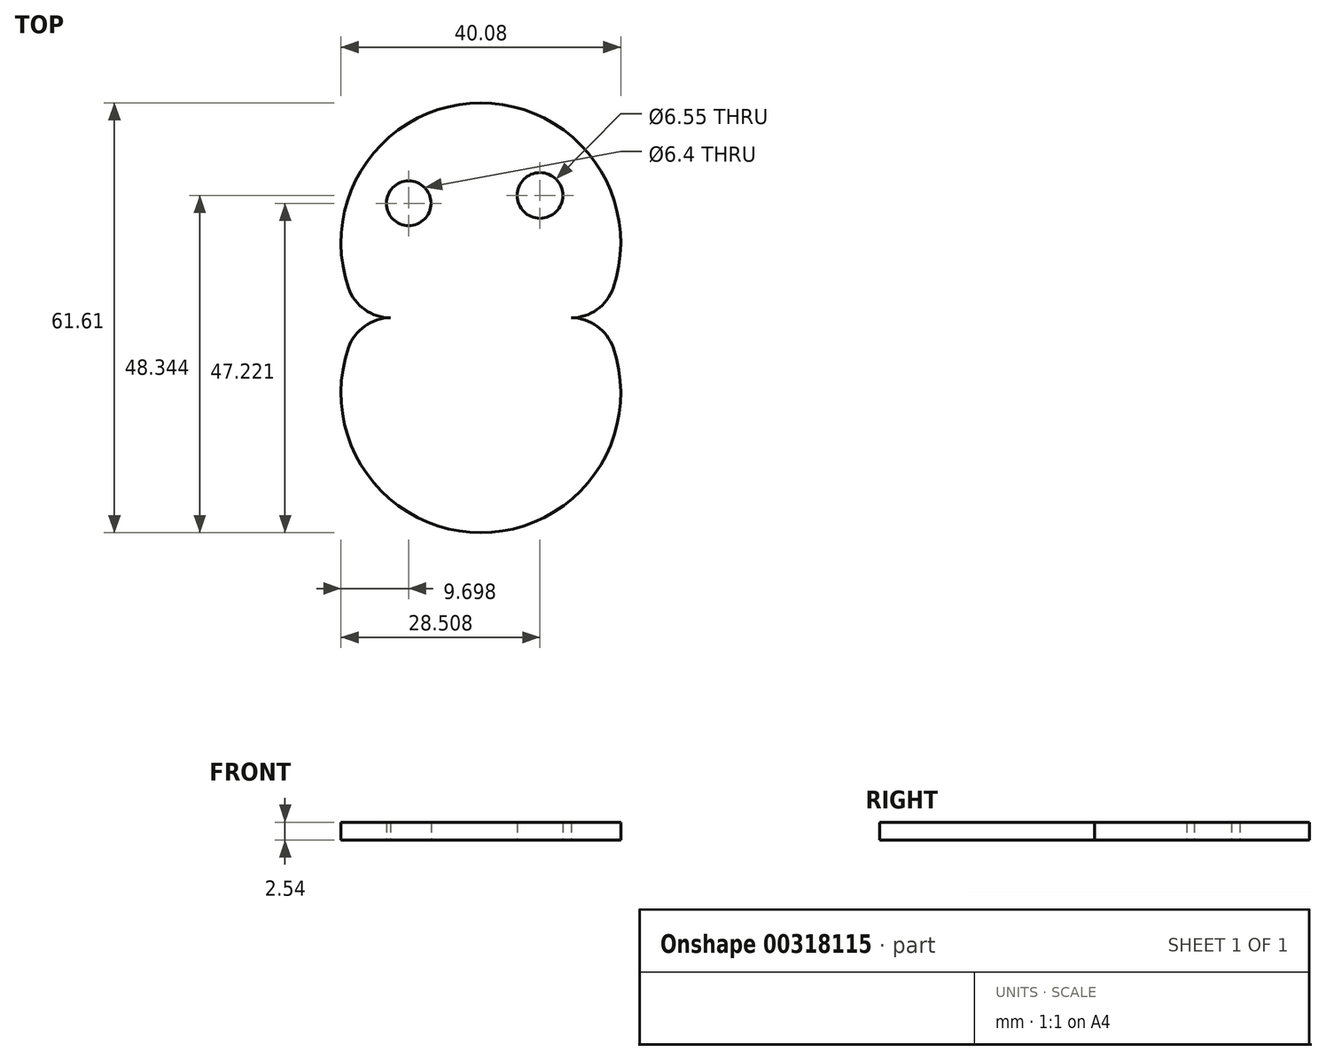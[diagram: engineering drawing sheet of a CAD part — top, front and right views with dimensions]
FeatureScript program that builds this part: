
annotation { "Feature Type Name" : "Feature", "Feature Type Description" : "" }
export const myFeature = defineFeature(function(context is Context, id is Id, definition is map)
    precondition{}
    {
        {
            var Q0;
            Q0=qCreatedBy(makeId("Top.planeOp"),FACE);
            var sketch = newSketch(context, id + "F0", { "sketchPlane" : qUnion([Q0])});
            skArc(sketch, "E0.0.startCap", {"start": v(-52.87, 18.11) * mm, "mid": v(-56.57, 19.3) * mm, "end": v(-58.88, 22.42) * mm});
            skArc(sketch, "E0.0.endCap", {"start": v(-20.94, 22.42) * mm, "mid": v(-23.26, 19.3) * mm, "end": v(-26.95, 18.11) * mm});
            skArc(sketch, "E0.1.startCap", {"start": v(-20.94, 22.42) * mm, "mid": v(-23.26, 19.3) * mm, "end": v(-26.95, 18.11) * mm});
            skArc(sketch, "E0.1.endCap", {"start": v(-52.87, 18.11) * mm, "mid": v(-56.57, 19.3) * mm, "end": v(-58.88, 22.42) * mm});
            skArc(sketch, "E0.1.right", {"start": v(-20.94, 22.42) * mm, "mid": v(-39.91, 48.92) * mm, "end": v(-58.88, 22.42) * mm});
            skArc(sketch, "E1.MirrorCS", {"start": v(-20.94, 13.81) * mm, "mid": v(-39.91, -12.7) * mm, "end": v(-58.88, 13.81) * mm});
            skArc(sketch, "E2.MirrorCS", {"start": v(-20.94, 13.81) * mm, "mid": v(-23.26, 16.93) * mm, "end": v(-26.95, 18.11) * mm});
            skArc(sketch, "E3.MirrorCS", {"start": v(-52.87, 18.11) * mm, "mid": v(-56.57, 16.93) * mm, "end": v(-58.88, 13.81) * mm});
            skFitSpline(sketch, "E4", {"points": [v(27.77, 29.98) * mm, v(33.3, 38.07) * mm, v(39.18, 29.61) * mm, v(48.74, 28.88) * mm, v(49.48, 20.05) * mm, v(38.44, 17.84) * mm, v(39.18, 10.48) * mm, v(42.86, 4.23) * mm, v(45.43, -6.44) * mm, v(41.02, -14.9) * mm, v(42.12, -21.52) * mm, v(34.4, -15.63) * mm, v(38.44, -8.28) * mm, v(30.72, -7.54) * mm, v(31.08, -22.26) * mm, v(24.46, -17.84) * mm, v(26.67, -5.33) * mm, v(19.68, -5.7) * mm, v(18.2, -20.05) * mm, v(13.43, -18.58) * mm, v(16, -6.44) * mm, v(12.7, -6.07) * mm, v(7.9, -18.58) * mm, v(7.9, -11.22) * mm, v(9.38, -5.33) * mm, v(14.53, 7.54) * mm, v(8.94, 10.65) * mm, v(9.53, 17.2) * mm, v(11.96, 10.85) * mm, v(18.94, 13.8) * mm, v(28.14, 7.9) * mm, v(31.08, 13.8) * mm, v(28.14, 22.62) * mm, v(23.73, 25.93) * mm, v(27.77, 29.98) * mm]});
            skCircle(sketch, "E5", {"center": v(-50.25, 34.53) * mm, "radius": 3.2 * mm});
            skCircle(sketch, "E6", {"center": v(-31.44, 35.65) * mm, "radius": 3.27 * mm});
            skPoint(sketch, "E7.center.orphan", {"position": v(36.22, 29.61) * mm});
            skCircle(sketch, "E8", {"center": v(36.22, 29.61) * mm, "radius": 1.77 * mm});
            skSolve(sketch);
        }
        {
            var Q0;
            Q0=makeQuery(id+"F0.imprint","IMPRINT",FACE,{"disambiguationData":[TD([[makeQuery(id+"F0.imprint","IMPRINT",EDGE,{"derivedFrom":sQuery(id+"F0.wireOp",EDGE,"E2.MirrorCS")}),1.0]])]});
            extrude(context, id + "F1", {"entities" : qUnion([Q0]), "depth" : 2.54 * mm});
        }
    });
